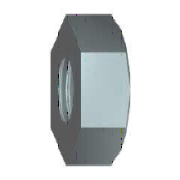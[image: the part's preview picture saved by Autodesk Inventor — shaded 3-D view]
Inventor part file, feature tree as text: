
AUTODESK INVENTOR PART (.ipt)
format: ipt  version: 2011 (Build 150229000, 229)  size: 165,376 bytes
history: native  units: mm
features: other x4, sketch x3, extrude x1, chamfer x1, revolve x1
ambient origin geometry x8: Origin, YZ Plane, XZ Plane, XY Plane, X Axis, Y Axis, Z Axis, Center Point
feature tree (10):
  extrude  "Extrusion1"  Depth=7.5mm
  chamfer  "Chamfer1"  Distance=0.625mm
  revolve  "Revolution1"  Angle=45.0deg
  other  "MSC_A1"
  other  "MSC_PT1"
  other  "MSC_PT2"
  other  "MSC_PF1"
  sketch  "Sketch1"  dims[d0=13.0mm d1=7.5mm]
  sketch  "Sketch2"  dims[d2=0.0mm]
  sketch  "Sketch3"  dims[d3=6.647mm d4=6.0mm d5=4.0mm d6=2.0mm d7=90.0deg d8=8.0mm d9=20.594885mm d10=0.625mm d11=2.0mm d12=45.0deg d15=90.0deg d16=0.0mm d17=0.0mm d18=0.0mm d19=0.0mm d21=0.0mm d22=0.0mm d23=0.0mm d32=6.5mm d33=30.0deg]
